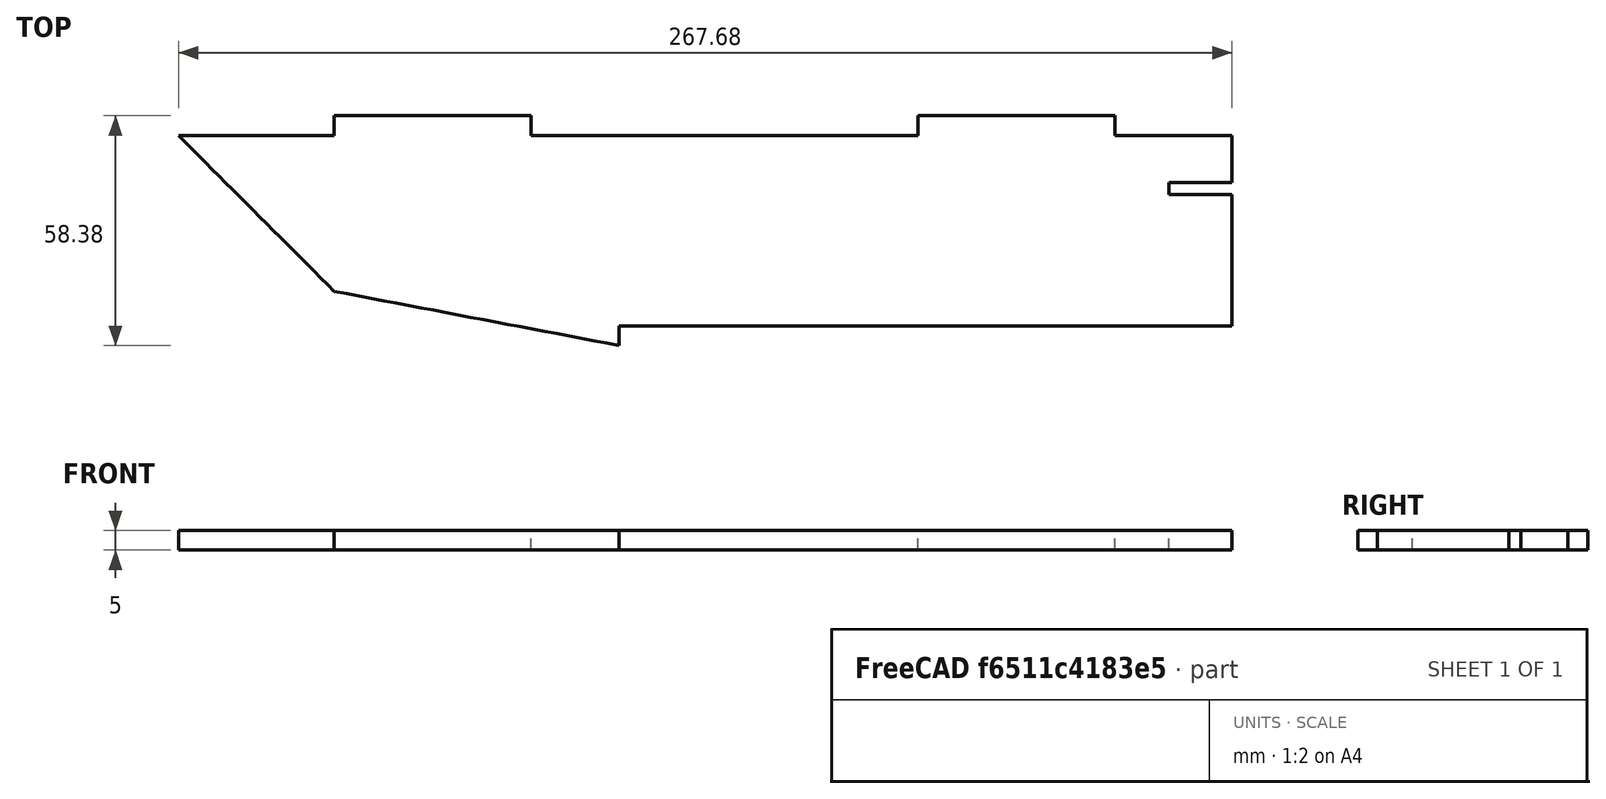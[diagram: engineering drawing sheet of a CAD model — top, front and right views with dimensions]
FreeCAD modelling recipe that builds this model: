
FCSTD DOCUMENT  (FreeCAD 0.19R)
Label: F-35_v2_parts_9
License: All rights reserved
LicenseURL: http://en.wikipedia.org/wiki/All_rights_reserved
objects: App::DocumentObjectGroup×2, PartDesign::CoordinateSystem×2, App::FeaturePython×1, Sketcher::SketchObject×1, PartDesign::Pad×1, PartDesign::Body×1, App::Part×1
note: 6 computed .brp shape members not serialized (recipe doc carries the construction recipe); baked Part::Feature solids carry a one-line shape summary decoded from their .brp

FEATURE [App::DocumentObjectGroup] Parts
FEATURE [PartDesign::CoordinateSystem] LCS_Origin
  AttacherType = Attacher::AttachEngine3D
  MapMode = 2
  Support = -> [X_Axis]
FEATURE [App::DocumentObjectGroup] Constraints
FEATURE [App::FeaturePython] Variables  # WARN: FeaturePython — macro-defined, semantics opaque (R4)
FEATURE [Sketcher::SketchObject] Sketch008
  FullyConstrained = false
  sketch-geometry (18):
    g0: BSplineCurve PolesCount=2 KnotsCount=2 Degree=1 IsPeriodic=0
    g1: BSplineCurve PolesCount=2 KnotsCount=2 Degree=1 IsPeriodic=0
    g2: BSplineCurve PolesCount=2 KnotsCount=2 Degree=1 IsPeriodic=0
    g3: BSplineCurve PolesCount=2 KnotsCount=2 Degree=1 IsPeriodic=0
    g4: BSplineCurve PolesCount=2 KnotsCount=2 Degree=1 IsPeriodic=0
    g5: BSplineCurve PolesCount=2 KnotsCount=2 Degree=1 IsPeriodic=0
    g6: BSplineCurve PolesCount=2 KnotsCount=2 Degree=1 IsPeriodic=0
    g7: BSplineCurve PolesCount=2 KnotsCount=2 Degree=1 IsPeriodic=0
    g8: BSplineCurve PolesCount=2 KnotsCount=2 Degree=1 IsPeriodic=0
    g9: BSplineCurve PolesCount=2 KnotsCount=2 Degree=1 IsPeriodic=0
    g10: BSplineCurve PolesCount=2 KnotsCount=2 Degree=1 IsPeriodic=0
    g11: BSplineCurve PolesCount=2 KnotsCount=2 Degree=1 IsPeriodic=0
    g12: BSplineCurve PolesCount=2 KnotsCount=2 Degree=1 IsPeriodic=0
    g13: BSplineCurve PolesCount=2 KnotsCount=2 Degree=1 IsPeriodic=0
    g14: BSplineCurve PolesCount=2 KnotsCount=2 Degree=1 IsPeriodic=0
    g15: BSplineCurve PolesCount=2 KnotsCount=2 Degree=1 IsPeriodic=0
    g16: BSplineCurve PolesCount=2 KnotsCount=2 Degree=1 IsPeriodic=0
    g17: BSplineCurve PolesCount=2 KnotsCount=2 Degree=1 IsPeriodic=0
FEATURE [PartDesign::Pad] Pad007
  Direction = (1,1,1)
  Length = 5
  Length2 = 100
  Profile = -> Sketch008
  Type = 0
FEATURE [PartDesign::Body] Body008  label="Part9"
  Group = -> [Sketch008,Pad007]
  Origin = -> Origin009
  Tip = -> Pad007
FEATURE [PartDesign::CoordinateSystem] LCS_1
  AttacherType = Attacher::AttachEngine3D
  MapMode = 7
  Placement = pos=(146.204,-486.427,0) rot=(0,1,0;3.14159rad)
  Support = -> [Pad007]
FEATURE [App::Part] Model
  Configuration = 0
  Group = -> [LCS_Origin,Constraints,Variables,Body008,LCS_1]
  Origin = -> Origin
  Type = Assembly4 Model
